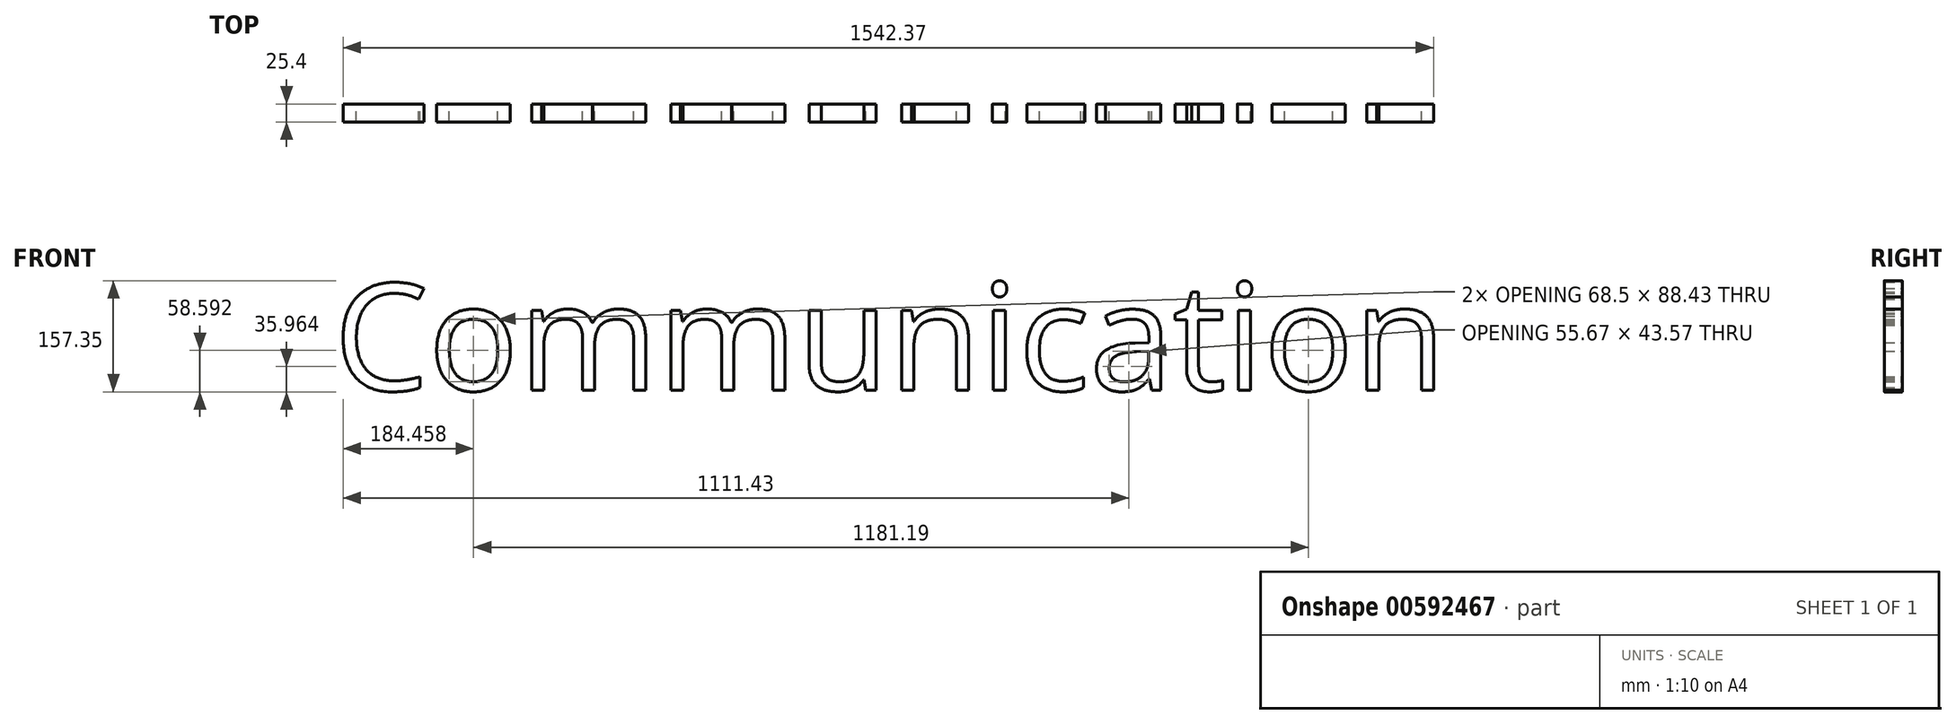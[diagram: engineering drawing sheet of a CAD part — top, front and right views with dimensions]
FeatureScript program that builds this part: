
annotation { "Feature Type Name" : "Feature", "Feature Type Description" : "" }
export const myFeature = defineFeature(function(context is Context, id is Id, definition is map)
    precondition{}
    {
        {
            var Q0;
            Q0=qCreatedBy(makeId("Front.planeOp"),FACE);
            var sketch = newSketch(context, id + "F0", { "sketchPlane" : qUnion([Q0])});
            skText(sketch, "E0", { "text": "Communication", "fontName": "OpenSans-Regular.ttf"});
            const initialGuessF0  = {"E0": [-0.0764, -0.07625, 1, 0, 0.15233]};
            skSetInitialGuess(sketch, initialGuessF0);
            skSolve(sketch);
        }
        {
            var Q0;
            Q0 = qSketchRegion(id + "F0", true);
            extrude(context, id + "F1", {"entities" : qUnion([Q0]), "depth" : 25.4 * mm, "offsetDistance" : 25.4 * mm});
        }
    });
